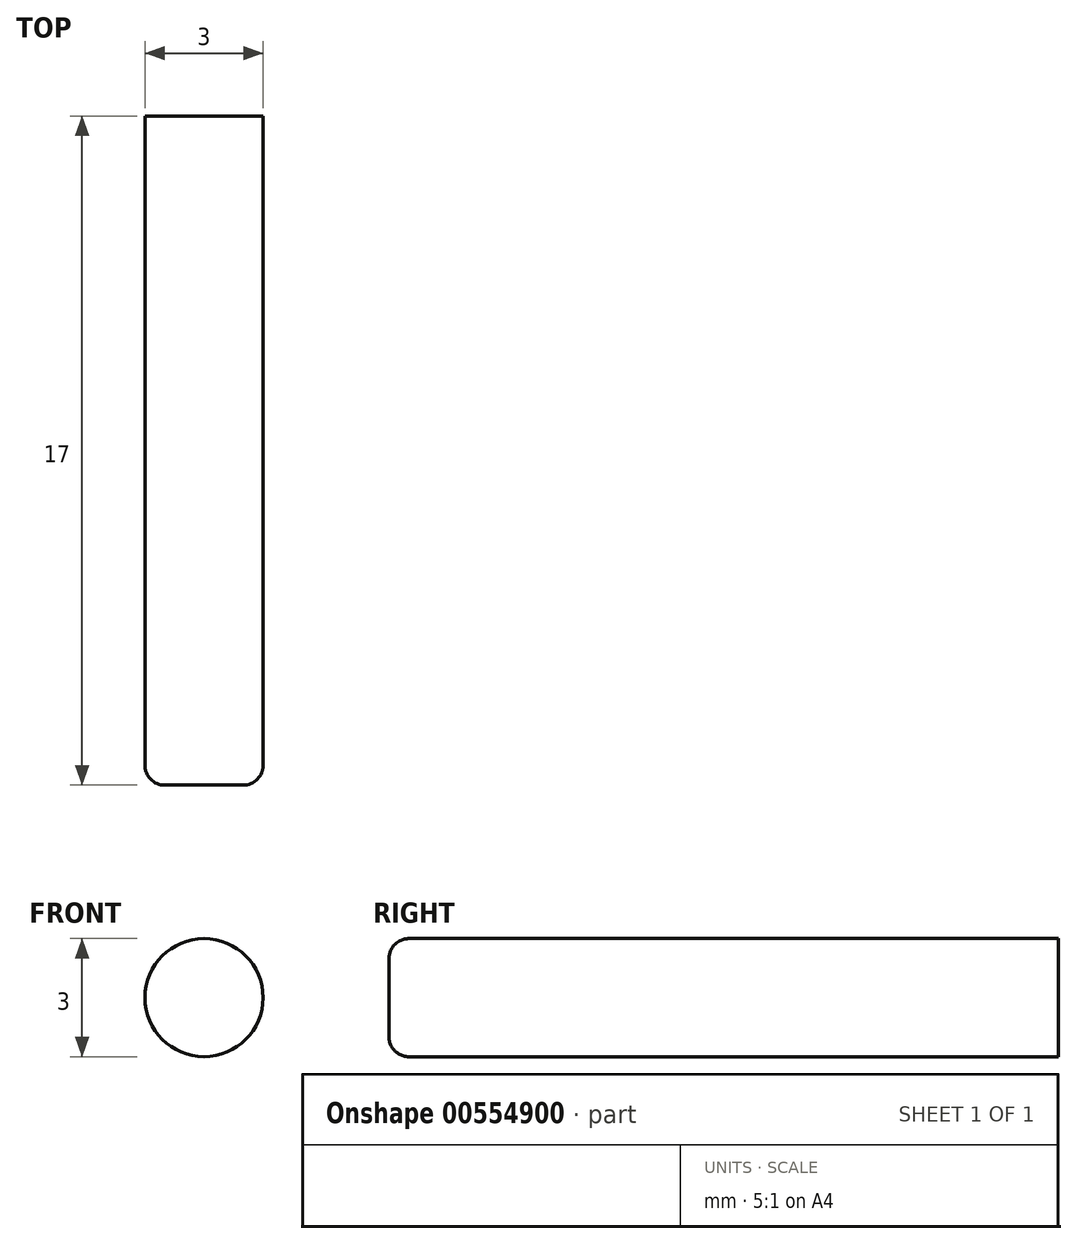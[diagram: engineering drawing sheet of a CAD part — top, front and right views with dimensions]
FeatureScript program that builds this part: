
annotation { "Feature Type Name" : "Feature", "Feature Type Description" : "" }
export const myFeature = defineFeature(function(context is Context, id is Id, definition is map)
    precondition{}
    {
        {
            var Q0;
            Q0=qCreatedBy(makeId("Front.planeOp"),FACE);
            var sketch = newSketch(context, id + "F0", { "sketchPlane" : qUnion([Q0])});
            skCircle(sketch, "E0", {"center": v(0, 0) * mm, "radius": 1.5 * mm});
            skSolve(sketch);
        }
        {
            var Q0;
            Q0=makeQuery(id+"F0.imprint","IMPRINT",FACE,{"disambiguationData":[TD([[makeQuery(id+"F0.imprint","IMPRINT",EDGE,{"derivedFrom":sQuery(id+"F0.wireOp",EDGE,"E0")}),1.0]])]});
            extrude(context, id + "F1", {"entities" : qUnion([Q0]), "depth" : 17 * mm, "offsetDistance" : 25 * mm});
        }
        {
            var Q0;
            Q0=makeQuery(id+"F1.opExtrude","CAP_EDGE",EDGE,{"disambiguationData":[OSD([sQuery(id+"F0.wireOp",EDGE,"E0")])],"isStart":false});
            fillet(context, id + "F2", {"entities" : qUnion([Q0]), "radius" : .5 * mm, "tangentPropagation" : true, "allowEdgeOverflow" : false});
        }
    });
